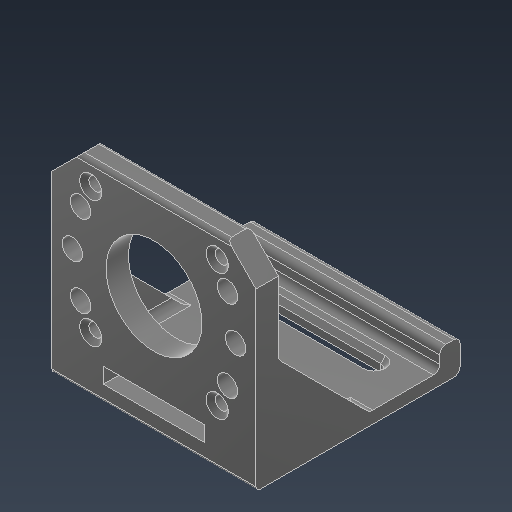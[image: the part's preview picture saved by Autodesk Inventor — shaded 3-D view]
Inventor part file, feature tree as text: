
AUTODESK INVENTOR PART (.ipt)
format: ipt  version: 2021.3 (Build 253353000, 353)  size: 303,616 bytes
history: native  units: mm
features: sketch x5, extrude x5, fillet x4, chamfer x2, mirror x1, hole x1, projected_geometry x1
ambient origin geometry x8: Origin, YZ Plane, XZ Plane, XY Plane, X Axis, Y Axis, Z Axis, Center Point
bodies: Solid1 (feature_tree)
feature tree (19):
  sketch  "Sketch1"  dims[d0=42.0mm d1=42.0mm d2=31.0mm d3=3.2mm d4=3.2mm d5=23.5mm d7=5.5mm d8=0.0mm]
  extrude  "Extrusion1"  Depth=3.2mm TaperAngle=0.0deg
  extrude  "Extrusion2"  Depth=4.0mm
  extrude  "Extrusion3"  Depth=50.0mm
  mirror  "Mirror1"
  fillet  "Fillet1"  Radius=3.0mm
  fillet  "Fillet2"  [1 undecoded]
  extrude  "Extrusion4"  Depth=2.0mm
  fillet  "Fillet3"  Radius=0.4mm
  extrude  "Extrusion5"  Depth=2.0mm TaperAngle=0.0deg
  hole  "Hole2"  [1 undecoded]
  chamfer  "Chamfer1"  Distance=5.0mm
  fillet  "Fillet4"  Radius=1.6mm
  chamfer  "Chamfer2"  Distance=1.6mm
  sketch  "Sketch2"  dims[d9=4.0mm d10=4.0mm]
  sketch  "Sketch5"  dims[d11=5.0mm d12=50.0mm d15=3.0mm d16=0.0mm d20=45.0deg]
  sketch  "Sketch6"  dims[d21=3.5mm d22=0.0mm d23=2.0mm d24=0.4mm]
  sketch  "Sketch8"  dims[d25=5.0mm d26=5.0mm d27=0.0mm d28=1.5mm d43=5.0mm d44=0.0mm d59=3.2mm d60=6.0mm d61=5.45mm d62=2.0mm d63=90.0deg d64=10.0mm d65=0.0mm d71=1.6mm d72=1.6mm d73=25.0mm d74=25.0mm d75=30.0mm d76=30.0mm d78=7.0mm d79=7.0mm d80=2.0mm d81=45.0deg d82=1.0mm d83=1.125mm d84=2.0mm d85=45.0deg d86=11.0mm d94=3.8mm d95=23.0mm d96=24.8mm d97=12.4mm d98=5.0mm d99=5.0mm d100=5.0mm d101=10.0mm d102=10.0mm d103=2.0mm d104=2.0mm d105=20.0mm]
  projected_geometry  "Projected Loop1"
note: 2 required parameter values undecoded (feature->parameter linkage not recoverable at this tier; creation-order binding heuristic only, values carry confidence <= 0.55)
